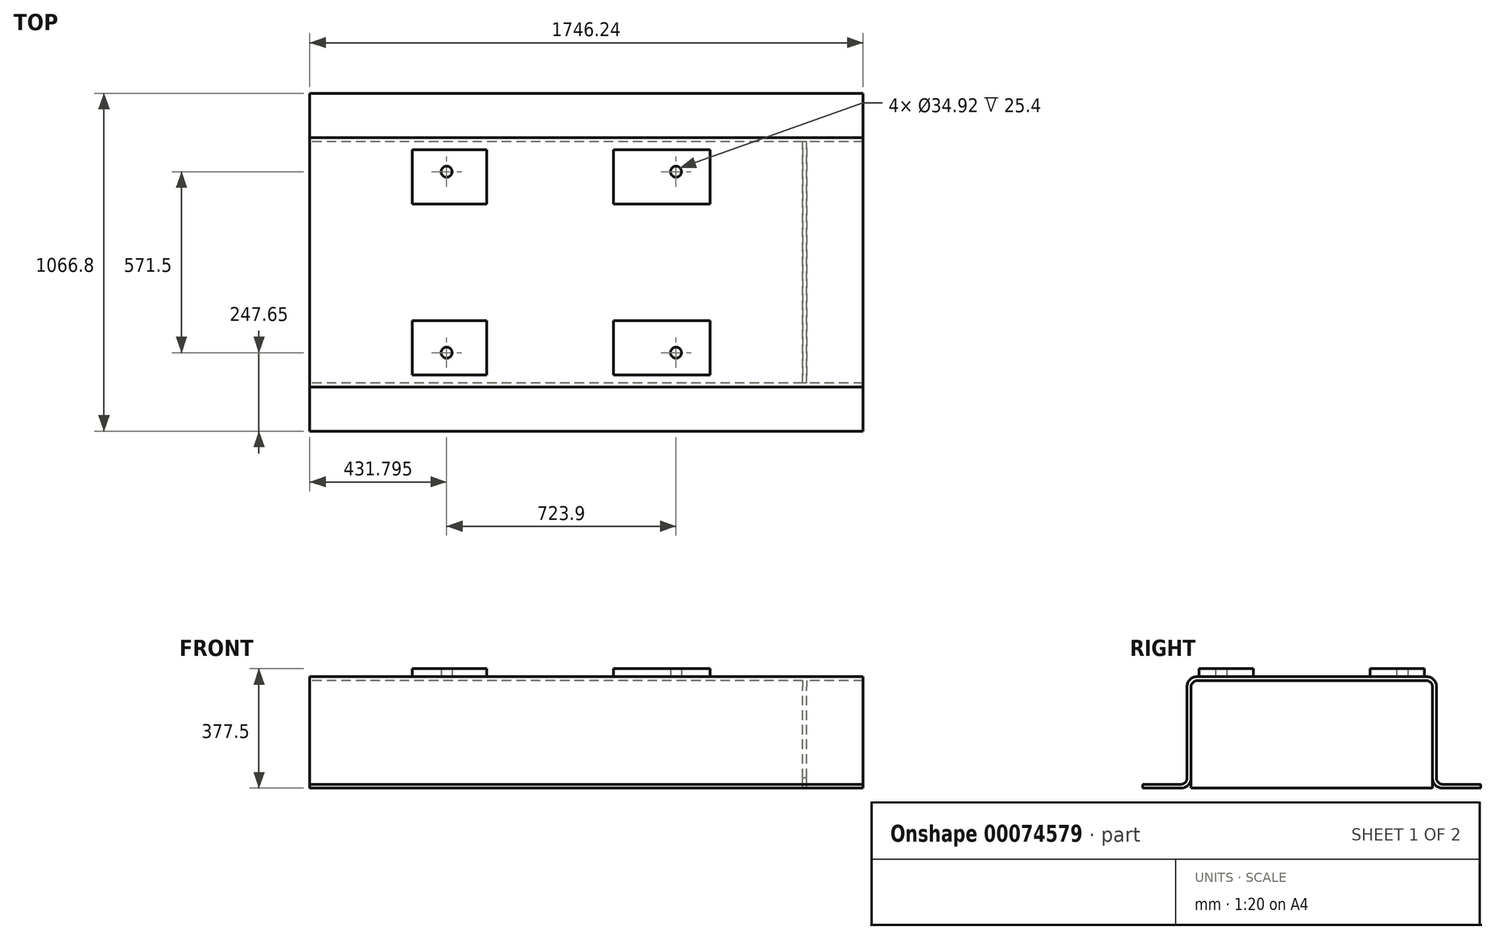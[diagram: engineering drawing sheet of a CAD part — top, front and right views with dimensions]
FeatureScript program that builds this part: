
annotation { "Feature Type Name" : "Feature", "Feature Type Description" : "" }
export const myFeature = defineFeature(function(context is Context, id is Id, definition is map)
    precondition{}
    {
        {
            var Q0;
            Q0=qCreatedBy(makeId("Right.planeOp"),FACE);
            var sketch = newSketch(context, id + "F0", { "sketchPlane" : qUnion([Q0])});
            skLineSegment(sketch, "E0", {"start": v(0, 473.15) * mm, "end": v(0, -407.2) * mm, "construction": true});
            skLineSegment(sketch, "E1.0", {"start": v(0, 352.55) * mm, "end": v(361.95, 352.55) * mm});
            skLineSegment(sketch, "E2.0", {"start": v(0, 339.85) * mm, "end": v(361.95, 339.85) * mm});
            skLineSegment(sketch, "E3.0", {"start": v(393.7, 320.8) * mm, "end": v(393.7, 31.75) * mm});
            skLineSegment(sketch, "E4.0", {"start": v(381, 320.8) * mm, "end": v(381, 32.2) * mm});
            skLineSegment(sketch, "E5.trimOffspring", {"start": v(412.75, 12.7) * mm, "end": v(520.7, 12.7) * mm});
            skLineSegment(sketch, "E6.trimOffspring", {"start": v(412.75, 0.45) * mm, "end": v(533.4, 0.45) * mm});
            skPoint(sketch, "E7.start.orphan", {"position": v(-520.7, 0) * mm});
            skArc(sketch, "E8.filletArc", {"start": v(381, 320.8) * mm, "mid": v(375.42, 334.27) * mm, "end": v(361.95, 339.85) * mm});
            skArc(sketch, "E9.filletArc", {"start": v(393.7, 31.75) * mm, "mid": v(399.28, 18.28) * mm, "end": v(412.75, 12.7) * mm});
            skArc(sketch, "E10.filletArc", {"start": v(381, 32.2) * mm, "mid": v(390.3, 9.75) * mm, "end": v(412.75, 0.45) * mm});
            skArc(sketch, "E11.filletArc", {"start": v(393.7, 320.8) * mm, "mid": v(384.4, 343.25) * mm, "end": v(361.95, 352.55) * mm});
            skLineSegment(sketch, "E12", {"start": v(0, 0) * mm, "end": v(739.32, 0) * mm, "construction": true});
            skLineSegment(sketch, "E13", {"start": v(533.4, 0.45) * mm, "end": v(533.4, 12.7) * mm});
            skLineSegment(sketch, "E14", {"start": v(533.4, 12.7) * mm, "end": v(516.63, 12.7) * mm});
            skLineSegment(sketch, "E15", {"start": v(0, 352.55) * mm, "end": v(0, 339.85) * mm});
            skArc(sketch, "E16.MirrorCS", {"start": v(-381, 320.8) * mm, "mid": v(-375.42, 334.27) * mm, "end": v(-361.95, 339.85) * mm});
            skArc(sketch, "E17.MirrorCS", {"start": v(-393.7, 31.75) * mm, "mid": v(-399.28, 18.28) * mm, "end": v(-412.75, 12.7) * mm});
            skArc(sketch, "E18.MirrorCS", {"start": v(-381, 32.2) * mm, "mid": v(-390.3, 9.75) * mm, "end": v(-412.75, 0.45) * mm});
            skLineSegment(sketch, "E19.MirrorCS", {"start": v(-533.4, 0.45) * mm, "end": v(-533.4, 12.7) * mm});
            skLineSegment(sketch, "E20.MirrorCS", {"start": v(-533.4, 12.7) * mm, "end": v(-516.63, 12.7) * mm});
            skArc(sketch, "E21.MirrorCS", {"start": v(-393.7, 320.8) * mm, "mid": v(-384.4, 343.25) * mm, "end": v(-361.95, 352.55) * mm});
            skLineSegment(sketch, "E22.MirrorCS", {"start": v(-412.75, 0.45) * mm, "end": v(-533.4, 0.45) * mm});
            skLineSegment(sketch, "E23.MirrorCS", {"start": v(-412.75, 12.7) * mm, "end": v(-520.7, 12.7) * mm});
            skLineSegment(sketch, "E24.MirrorCS", {"start": v(-381, 320.8) * mm, "end": v(-381, 32.2) * mm});
            skLineSegment(sketch, "E25.MirrorCS", {"start": v(0, 0) * mm, "end": v(-739.32, 0) * mm, "construction": true});
            skLineSegment(sketch, "E26.MirrorCS", {"start": v(0, 352.55) * mm, "end": v(-361.95, 352.55) * mm});
            skLineSegment(sketch, "E27.MirrorCS", {"start": v(-393.7, 320.8) * mm, "end": v(-393.7, 31.75) * mm});
            skLineSegment(sketch, "E28.MirrorCS", {"start": v(0, 339.85) * mm, "end": v(-361.95, 339.85) * mm});
            skSolve(sketch);
        }
        {
            var Q0;
            Q0=makeQuery(id+"F0.imprint","IMPRINT",FACE,{"disambiguationData":[TD([[makeQuery(id+"F0.imprint","IMPRINT",EDGE,{"derivedFrom":sQuery(id+"F0.wireOp",EDGE,"E15")}),-1.0]])]});
            var Q1;
            Q1=makeQuery(id+"F0.imprint","IMPRINT",FACE,{"disambiguationData":[TD([[makeQuery(id+"F0.imprint","IMPRINT",EDGE,{"derivedFrom":sQuery(id+"F0.wireOp",EDGE,"E1.0")}),-1.0]])]});
            extrude(context, id + "F1", {"entities" : qUnion([Q0, Q1]), "endBound" : BoundingType.SYMMETRIC, "depth" : 1746.25 * mm});
        }
        {
            var Q0;
            Q0=makeQuery(id+"F1.opExtrude","SWEPT_FACE",FACE,{"disambiguationData":[OSD([sQuery(id+"F0.wireOp",EDGE,"E2.0"),sQuery(id+"F0.wireOp",EDGE,"E28.MirrorCS")])]});
            var sketch = newSketch(context, id + "F2", { "sketchPlane" : qUnion([Q0])});
            skLineSegment(sketch, "E29.0", {"start": v(695.32, -381) * mm, "end": v(695.32, 381) * mm});
            skLineSegment(sketch, "E30.0", {"start": v(682.62, -381) * mm, "end": v(682.62, 381) * mm});
            skLineSegment(sketch, "E31.0", {"start": v(695.32, 381) * mm, "end": v(682.62, 381) * mm});
            skLineSegment(sketch, "E32.0", {"start": v(695.32, -381) * mm, "end": v(682.62, -381) * mm});
            skPoint(sketch, "E33.orphan", {"position": v(-873.12, 381) * mm});
            skPoint(sketch, "E34.orphan", {"position": v(873.12, 381) * mm});
            skPoint(sketch, "E35.orphan", {"position": v(-873.12, -381) * mm});
            skPoint(sketch, "E36.orphan", {"position": v(873.12, -381) * mm});
            skSolve(sketch);
        }
        {
            var Q0;
            Q0 = qSketchRegion(id + "F2", true);
            var Q1;
            Q1=makeQuery(id+"F1.opExtrude","SWEPT_FACE",FACE,{"disambiguationData":[OSD([sQuery(id+"F0.wireOp",EDGE,"E6.trimOffspring")])]});
            extrude(context, id + "F3", {"entities" : qUnion([Q0]), "operationType" : NewBodyOperationType.ADD, "endBound" : BoundingType.UP_TO_SURFACE, "endBoundEntityFace" : qUnion([Q1]), "depth" : 25.4 * mm});
        }
        {
            var Q0;
            Q0=makeQuery(id+"F1.opExtrude","SWEPT_FACE",FACE,{"disambiguationData":[OSD([sQuery(id+"F0.wireOp",EDGE,"E1.0"),sQuery(id+"F0.wireOp",EDGE,"E26.MirrorCS")])]});
            var sketch = newSketch(context, id + "F4", { "sketchPlane" : qUnion([Q0])});
            skLineSegment(sketch, "E37.0", {"start": v(-1673.23, 361.95) * mm, "end": v(-1673.23, -1102.1) * mm, "construction": true});
            skLineSegment(sketch, "E38.0", {"start": v(-1209.68, 361.95) * mm, "end": v(-1209.68, -1102.1) * mm, "construction": true});
            skLineSegment(sketch, "E39.0", {"start": v(-79.38, 361.95) * mm, "end": v(-79.38, -1102.1) * mm, "construction": true});
            skLineSegment(sketch, "E40.0", {"start": v(644.52, 361.95) * mm, "end": v(644.52, -1102.1) * mm, "construction": true});
            skLineSegment(sketch, "E41", {"start": v(-1510, 0) * mm, "end": v(1125.96, 0) * mm, "construction": true});
            skPoint(sketch, "E41.endSnap0", {"position": v(873.12, 0) * mm});
            skLineSegment(sketch, "E42.0", {"start": v(85.72, 361.95) * mm, "end": v(85.72, -1102.1) * mm, "construction": true});
            skLineSegment(sketch, "E43.0", {"start": v(390.52, 361.95) * mm, "end": v(390.52, -1102.1) * mm, "construction": true});
            skLineSegment(sketch, "E44.0", {"start": v(-314.33, 361.95) * mm, "end": v(-314.33, -1102.1) * mm, "construction": true});
            skLineSegment(sketch, "E45.0", {"start": v(-549.28, 361.95) * mm, "end": v(-549.28, -1102.1) * mm, "construction": true});
            skLineSegment(sketch, "E46.0", {"start": v(-1510, 184.15) * mm, "end": v(1125.96, 184.15) * mm, "construction": true});
            skLineSegment(sketch, "E47.0", {"start": v(-1510, 355.6) * mm, "end": v(1125.96, 355.6) * mm, "construction": true});
            skLineSegment(sketch, "E48.bottom", {"start": v(-549.28, 355.6) * mm, "end": v(-314.33, 355.6) * mm});
            skLineSegment(sketch, "E48.top", {"start": v(-549.28, 184.15) * mm, "end": v(-314.33, 184.15) * mm});
            skLineSegment(sketch, "E48.left", {"start": v(-549.28, 355.6) * mm, "end": v(-549.28, 184.15) * mm});
            skLineSegment(sketch, "E48.right", {"start": v(-314.33, 355.6) * mm, "end": v(-314.33, 184.15) * mm});
            skLineSegment(sketch, "E49.bottom", {"start": v(390.52, 355.6) * mm, "end": v(85.72, 355.6) * mm});
            skLineSegment(sketch, "E49.top", {"start": v(390.52, 184.15) * mm, "end": v(85.72, 184.15) * mm});
            skLineSegment(sketch, "E49.left", {"start": v(390.52, 355.6) * mm, "end": v(390.52, 184.15) * mm});
            skLineSegment(sketch, "E49.right", {"start": v(85.72, 355.6) * mm, "end": v(85.72, 184.15) * mm});
            skLineSegment(sketch, "E50.0", {"start": v(-1510, 285.75) * mm, "end": v(1125.96, 285.75) * mm, "construction": true});
            skLineSegment(sketch, "E51.0", {"start": v(-441.33, 361.95) * mm, "end": v(-441.33, -1102.1) * mm, "construction": true});
            skLineSegment(sketch, "E52.0", {"start": v(282.57, 361.95) * mm, "end": v(282.57, -1102.1) * mm, "construction": true});
            skCircle(sketch, "E53", {"center": v(-441.33, 285.75) * mm, "radius": 17.46 * mm});
            skCircle(sketch, "E54", {"center": v(282.57, 285.75) * mm, "radius": 17.46 * mm});
            skLineSegment(sketch, "E55.MirrorCS", {"start": v(390.52, -184.15) * mm, "end": v(85.72, -184.15) * mm});
            skLineSegment(sketch, "E56.MirrorCS", {"start": v(390.52, -355.6) * mm, "end": v(390.52, -184.15) * mm});
            skCircle(sketch, "E57.MirrorC", {"center": v(-441.33, -285.75) * mm, "radius": 17.46 * mm});
            skLineSegment(sketch, "E58.MirrorCS", {"start": v(85.72, -355.6) * mm, "end": v(85.72, -184.15) * mm});
            skLineSegment(sketch, "E59.MirrorCS", {"start": v(-549.28, -355.6) * mm, "end": v(-549.28, -184.15) * mm});
            skCircle(sketch, "E60.MirrorC", {"center": v(282.57, -285.75) * mm, "radius": 17.46 * mm});
            skLineSegment(sketch, "E61.MirrorCS", {"start": v(390.52, -355.6) * mm, "end": v(85.72, -355.6) * mm});
            skLineSegment(sketch, "E62.MirrorCS", {"start": v(-314.33, -355.6) * mm, "end": v(-314.33, -184.15) * mm});
            skLineSegment(sketch, "E63.MirrorCS", {"start": v(-549.28, -355.6) * mm, "end": v(-314.33, -355.6) * mm});
            skLineSegment(sketch, "E64.MirrorCS", {"start": v(-549.28, -184.15) * mm, "end": v(-314.33, -184.15) * mm});
            skSolve(sketch);
        }
        {
            var Q0;
            Q0 = qSketchRegion(id + "F4", true);
            extrude(context, id + "F5", {"entities" : qUnion([Q0]), "operationType" : NewBodyOperationType.ADD, "depth" : 25.4 * mm});
        }
    });
